# Revit family: 306_R2_-_-S_
name_source: partatom
category: Pipe Accessories
units: mm (PartAtom-declared; Revit-internal decimal feet)

## family parameters
Always vertical = Yes
Cut with Voids When Loaded = No
Part Type = Valve - Breaks Into
Round Connector Dimension = Use Diameter
Shared = No
Work Plane-Based = No

## types (19) — shared parameters
B33 = 4 mm  [stored 0.0131234 ft]
B4 = 11 mm
BB = 23 mm
CAT0 = Yes
Description = Characterised control valve, 2-way, Internal thread
FD1 = 23 mm
FD4 = 11 mm
H2 = 8 mm  [stored 0.0262467 ft]
L2D_Min = 3048 mm
Manufacturer = Belimo
QmdConnectorList = 301;D;302;D
magiPartTypeId = 306
magiProductFamilyId = R2*-*-S*
zero-valued in all types: MC_Default_elevation

## per-type parameters (varying)
| type | CenSd_D11_6 | D | D11 | FD | H | H1 | H11 | H1__ve | L1 | L2 | L2D | L3 | LL | W2D |
| R2015-P25-S1 | 10 mm  [stored 0.0328084 ft] | 15 mm | 12 mm  [stored 0.0393701 ft] | 26 mm | 35 mm  [stored 0.114829 ft] | 4 mm  [stored 0.0131234 ft] | 31 mm | -4 mm | 18 mm | 35 mm  [stored 0.114829 ft] | 67 mm | 15 mm  [stored 0.0492126 ft] | 34 mm  [stored 0.111549 ft] | 15 mm  [stored 0.0492126 ft] |
| R2050-40-S4 | 35 mm  [stored 0.114829 ft] | 50 mm | 40 mm  [stored 0.131234 ft] | 85 mm | 56 mm | 7 mm  [stored 0.0229659 ft] | 49 mm  [stored 0.160761 ft] | -7 mm  [stored -0.0229659 ft] | 33 mm | 65 mm | 125 mm | 27 mm | 63 mm | 50 mm  [stored 0.164042 ft] |
| R2050-25-S4 | 35 mm  [stored 0.114829 ft] | 50 mm | 40 mm  [stored 0.131234 ft] | 85 mm | 56 mm | 7 mm  [stored 0.0229659 ft] | 49 mm  [stored 0.160761 ft] | -7 mm  [stored -0.0229659 ft] | 33 mm | 65 mm | 125 mm | 27 mm | 63 mm | 50 mm  [stored 0.164042 ft] |
| R2040-25-S3 | 28 mm  [stored 0.0918635 ft] | 40 mm | 32 mm  [stored 0.104987 ft] | 68 mm | 51 mm | 6 mm  [stored 0.019685 ft] | 44 mm  [stored 0.144357 ft] | -6 mm  [stored -0.019685 ft] | 30 mm  [stored 0.0984252 ft] | 57 mm | 111 mm | 24 mm | 56 mm | 40 mm  [stored 0.131234 ft] |
| R2040-16-S3 | 28 mm  [stored 0.0918635 ft] | 40 mm | 32 mm  [stored 0.104987 ft] | 68 mm | 51 mm | 6 mm  [stored 0.019685 ft] | 44 mm  [stored 0.144357 ft] | -6 mm  [stored -0.019685 ft] | 30 mm  [stored 0.0984252 ft] | 57 mm | 111 mm | 24 mm | 56 mm | 40 mm  [stored 0.131234 ft] |
| R2032-16-S3 | 22 mm | 32 mm | 26 mm | 54 mm | 51 mm | 6 mm  [stored 0.019685 ft] | 44 mm  [stored 0.144357 ft] | -6 mm  [stored -0.019685 ft] | 28 mm  [stored 0.0918635 ft] | 54 mm | 105 mm | 23 mm | 53 mm | 32 mm  [stored 0.104987 ft] |
| R2025-16-S2 | 17 mm | 25 mm | 20 mm  [stored 0.0656168 ft] | 43 mm | 46 mm  [stored 0.150919 ft] | 6 mm  [stored 0.019685 ft] | 40 mm  [stored 0.131234 ft] | -6 mm  [stored -0.019685 ft] | 23 mm | 45 mm | 87 mm | 19 mm | 44 mm  [stored 0.144357 ft] | 25 mm  [stored 0.082021 ft] |
| R2025-10-S2 | 17 mm | 25 mm | 20 mm  [stored 0.0656168 ft] | 43 mm | 46 mm  [stored 0.150919 ft] | 6 mm  [stored 0.019685 ft] | 40 mm  [stored 0.131234 ft] | -6 mm  [stored -0.019685 ft] | 23 mm | 45 mm | 87 mm | 19 mm | 44 mm  [stored 0.144357 ft] | 25 mm  [stored 0.082021 ft] |
| R2025-6P3-S2 | 17 mm | 25 mm | 20 mm  [stored 0.0656168 ft] | 43 mm | 46 mm  [stored 0.150919 ft] | 6 mm  [stored 0.019685 ft] | 40 mm  [stored 0.131234 ft] | -6 mm  [stored -0.019685 ft] | 23 mm | 45 mm | 87 mm | 19 mm | 44 mm  [stored 0.144357 ft] | 25 mm  [stored 0.082021 ft] |
| R2020-8P6-S2 | 14 mm  [stored 0.0459318 ft] | 20 mm | 16 mm  [stored 0.0524934 ft] | 34 mm  [stored 0.111549 ft] | 46 mm  [stored 0.150919 ft] | 6 mm  [stored 0.019685 ft] | 40 mm  [stored 0.131234 ft] | -6 mm  [stored -0.019685 ft] | 21 mm | 40 mm  [stored 0.131234 ft] | 78 mm | 17 mm | 39 mm  [stored 0.127953 ft] | 20 mm  [stored 0.0656168 ft] |
| R2020-6P3-S2 | 14 mm  [stored 0.0459318 ft] | 20 mm | 16 mm  [stored 0.0524934 ft] | 34 mm  [stored 0.111549 ft] | 46 mm  [stored 0.150919 ft] | 6 mm  [stored 0.019685 ft] | 40 mm  [stored 0.131234 ft] | -6 mm  [stored -0.019685 ft] | 21 mm | 40 mm  [stored 0.131234 ft] | 78 mm | 17 mm | 39 mm  [stored 0.127953 ft] | 20 mm  [stored 0.0656168 ft] |
| R2020-4-S2 | 14 mm  [stored 0.0459318 ft] | 20 mm | 16 mm  [stored 0.0524934 ft] | 34 mm  [stored 0.111549 ft] | 46 mm  [stored 0.150919 ft] | 6 mm  [stored 0.019685 ft] | 40 mm  [stored 0.131234 ft] | -6 mm  [stored -0.019685 ft] | 21 mm | 40 mm  [stored 0.131234 ft] | 78 mm | 17 mm | 39 mm  [stored 0.127953 ft] | 20 mm  [stored 0.0656168 ft] |
| R2015-6P3-S1 | 10 mm  [stored 0.0328084 ft] | 15 mm | 12 mm  [stored 0.0393701 ft] | 26 mm | 44 mm  [stored 0.144357 ft] | 6 mm  [stored 0.019685 ft] | 39 mm  [stored 0.127953 ft] | -6 mm  [stored -0.019685 ft] | 18 mm | 35 mm  [stored 0.114829 ft] | 67 mm | 15 mm  [stored 0.0492126 ft] | 34 mm  [stored 0.111549 ft] | 15 mm  [stored 0.0492126 ft] |
| R2015-4-S1 | 10 mm  [stored 0.0328084 ft] | 15 mm | 12 mm  [stored 0.0393701 ft] | 26 mm | 44 mm  [stored 0.144357 ft] | 6 mm  [stored 0.019685 ft] | 39 mm  [stored 0.127953 ft] | -6 mm  [stored -0.019685 ft] | 18 mm | 35 mm  [stored 0.114829 ft] | 67 mm | 15 mm  [stored 0.0492126 ft] | 34 mm  [stored 0.111549 ft] | 15 mm  [stored 0.0492126 ft] |
| R2015-2P5-S1 | 10 mm  [stored 0.0328084 ft] | 15 mm | 12 mm  [stored 0.0393701 ft] | 26 mm | 44 mm  [stored 0.144357 ft] | 6 mm  [stored 0.019685 ft] | 39 mm  [stored 0.127953 ft] | -6 mm  [stored -0.019685 ft] | 18 mm | 35 mm  [stored 0.114829 ft] | 67 mm | 15 mm  [stored 0.0492126 ft] | 34 mm  [stored 0.111549 ft] | 15 mm  [stored 0.0492126 ft] |
| R2015-1P6-S1 | 10 mm  [stored 0.0328084 ft] | 15 mm | 12 mm  [stored 0.0393701 ft] | 26 mm | 35 mm  [stored 0.114829 ft] | 4 mm  [stored 0.0131234 ft] | 31 mm | -4 mm | 18 mm | 35 mm  [stored 0.114829 ft] | 67 mm | 15 mm  [stored 0.0492126 ft] | 34 mm  [stored 0.111549 ft] | 15 mm  [stored 0.0492126 ft] |
| R2015-1-S1 | 10 mm  [stored 0.0328084 ft] | 15 mm | 12 mm  [stored 0.0393701 ft] | 26 mm | 35 mm  [stored 0.114829 ft] | 4 mm  [stored 0.0131234 ft] | 31 mm | -4 mm | 18 mm | 35 mm  [stored 0.114829 ft] | 67 mm | 15 mm  [stored 0.0492126 ft] | 34 mm  [stored 0.111549 ft] | 15 mm  [stored 0.0492126 ft] |
| R2015-P63-S1 | 10 mm  [stored 0.0328084 ft] | 15 mm | 12 mm  [stored 0.0393701 ft] | 26 mm | 35 mm  [stored 0.114829 ft] | 4 mm  [stored 0.0131234 ft] | 31 mm | -4 mm | 18 mm | 35 mm  [stored 0.114829 ft] | 67 mm | 15 mm  [stored 0.0492126 ft] | 34 mm  [stored 0.111549 ft] | 15 mm  [stored 0.0492126 ft] |
| R2015-P4-S1 | 10 mm  [stored 0.0328084 ft] | 15 mm | 12 mm  [stored 0.0393701 ft] | 26 mm | 35 mm  [stored 0.114829 ft] | 4 mm  [stored 0.0131234 ft] | 31 mm | -4 mm | 18 mm | 35 mm  [stored 0.114829 ft] | 67 mm | 15 mm  [stored 0.0492126 ft] | 34 mm  [stored 0.111549 ft] | 15 mm  [stored 0.0492126 ft] |

note: column(s) folded — value = type name in every type: magiProductCode, magiProductId

note: [stored X ft] marks values corroborated as IEEE doubles in the binary element streams (Revit-internal decimal feet)

## geometry (parser evidence)
native form markers: Sweep x1
no freeform markers — native parametric forms only
